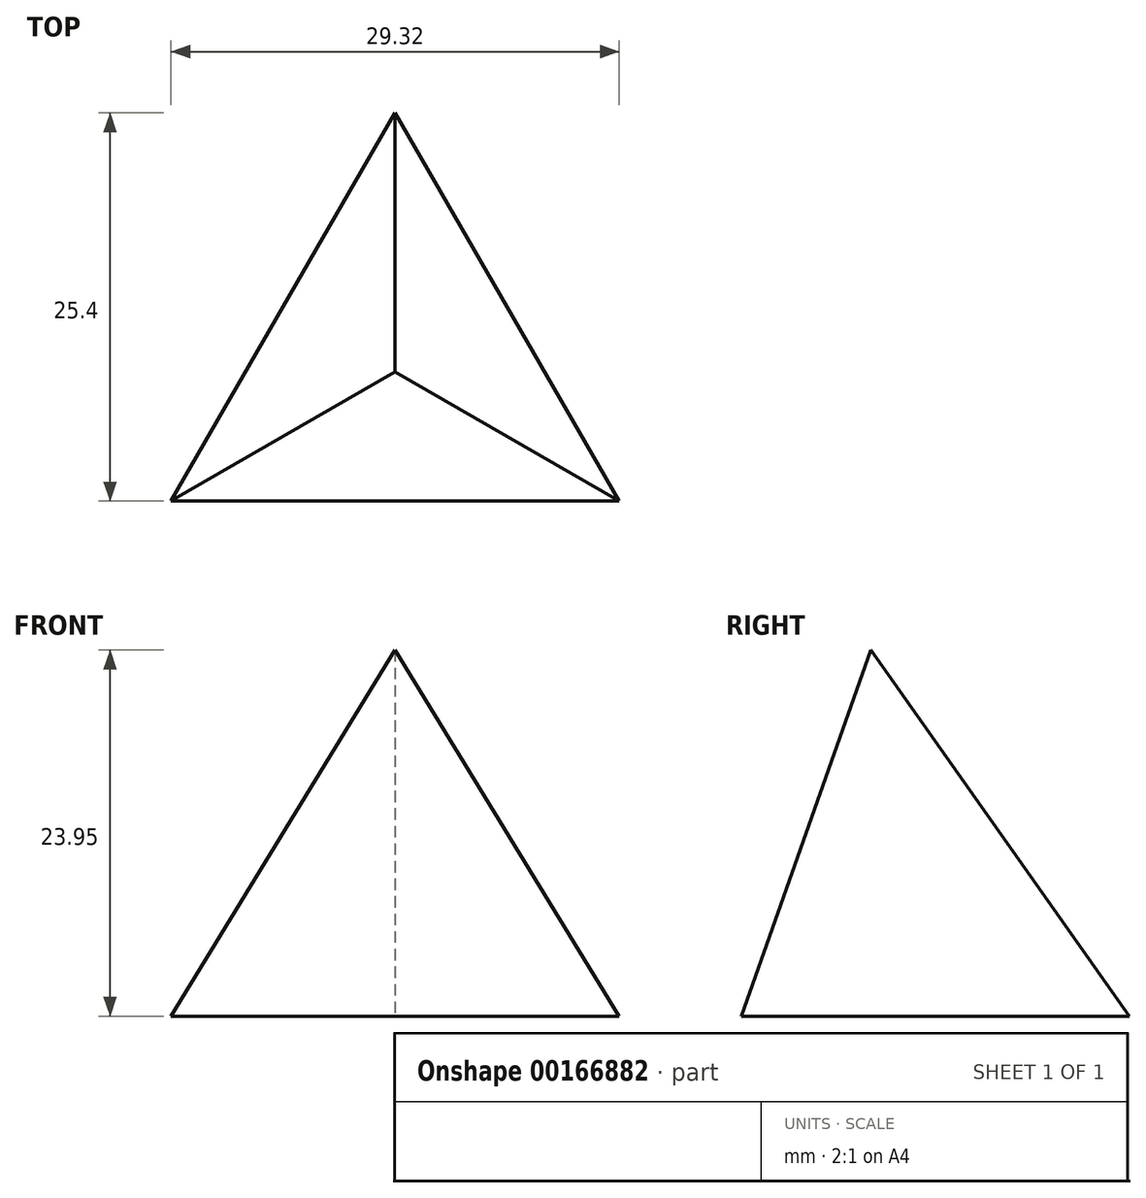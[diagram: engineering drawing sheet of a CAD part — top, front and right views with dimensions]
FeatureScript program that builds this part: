
annotation { "Feature Type Name" : "Feature", "Feature Type Description" : "" }
export const myFeature = defineFeature(function(context is Context, id is Id, definition is map)
    precondition{}
    {
        {
            var Q0;
            Q0=qCreatedBy(makeId("Top.planeOp"),FACE);
            var sketch = newSketch(context, id + "F0", { "sketchPlane" : qUnion([Q0])});
            skLineSegment(sketch, "E0", {"start": v(-14.66, 0) * mm, "end": v(14.66, 0) * mm});
            skLineSegment(sketch, "E1", {"start": v(14.66, 0) * mm, "end": v(0, 25.4) * mm});
            skLineSegment(sketch, "E2", {"start": v(0, 25.4) * mm, "end": v(-14.66, 0) * mm});
            skSolve(sketch);
        }
        {
            var Q0;
            Q0=makeQuery(id+"F0.imprint","IMPRINT",FACE,{"disambiguationData":[TD([[makeQuery(id+"F0.imprint","IMPRINT",EDGE,{"derivedFrom":sQuery(id+"F0.wireOp",EDGE,"E0")}),1.0]])]});
            extrude(context, id + "F1", {"entities" : qUnion([Q0]), "depth" : 25.4 * mm, "hasDraft" : true, "draftAngle" : 90 * degree - atan(2 * (2 ^ 0.5)), "draftPullDirection" : true});
        }
    });
